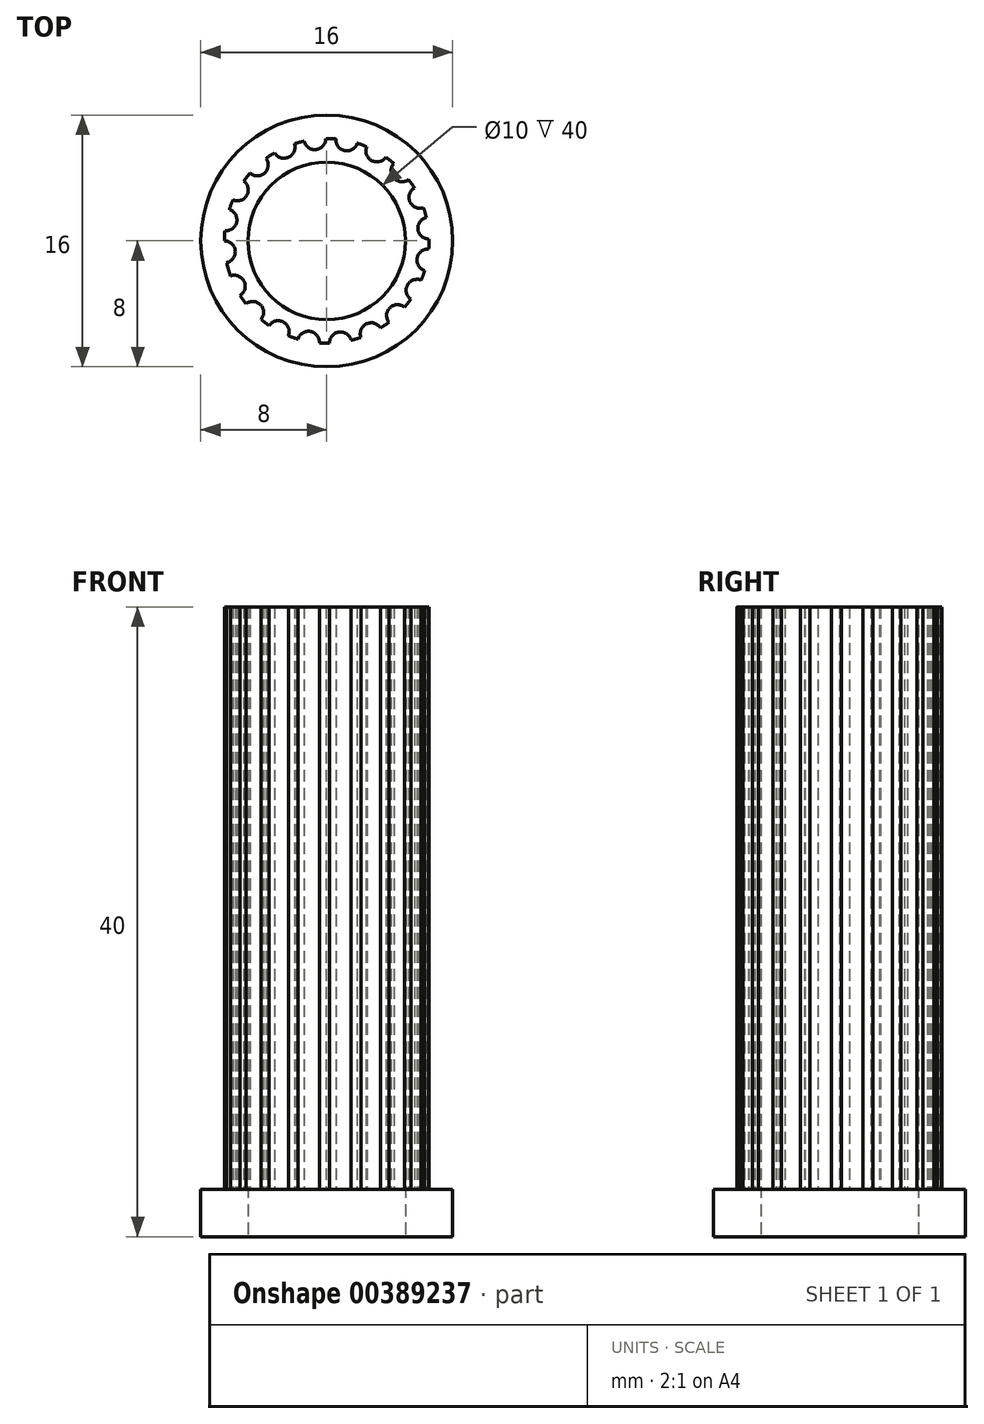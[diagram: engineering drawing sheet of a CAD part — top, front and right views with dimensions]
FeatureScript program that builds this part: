
annotation { "Feature Type Name" : "Feature", "Feature Type Description" : "" }
export const myFeature = defineFeature(function(context is Context, id is Id, definition is map)
    precondition{}
    {
        {
            var Q0;
            Q0=qCreatedBy(makeId("Top.planeOp"),FACE);
            var sketch = newSketch(context, id + "F0", { "sketchPlane" : qUnion([Q0])});
            skCircle(sketch, "E0", {"center": v(0, 0) * mm, "radius": 8 * mm});
            skArc(sketch, "E1", {"start": v(-4.87, 4.3) * mm, "mid": v(-5.08, 4.06) * mm, "end": v(-5.27, 3.8) * mm});
            skCircle(sketch, "E2", {"center": v(0, 0) * mm, "radius": 5 * mm});
            skArc(sketch, "E3", {"start": v(-6.35, -1.38) * mm, "mid": v(-5.8, -0.62) * mm, "end": v(-6.5, 0) * mm});
            skArc(sketch, "E4.1.0", {"start": v(-6.47, 0.64) * mm, "mid": v(-5.72, 1.2) * mm, "end": v(-6.19, 2) * mm});
            skArc(sketch, "E4.2.0", {"start": v(-5.96, 2.6) * mm, "mid": v(-5.08, 2.9) * mm, "end": v(-5.27, 3.8) * mm});
            skArc(sketch, "E4.3.0", {"start": v(-4.87, 4.3) * mm, "mid": v(-3.94, 4.31) * mm, "end": v(-3.85, 5.24) * mm});
            skArc(sketch, "E4.4.0", {"start": v(-3.31, 5.6) * mm, "mid": v(-2.43, 5.32) * mm, "end": v(-2.05, 6.17) * mm});
            skArc(sketch, "E4.5.0", {"start": v(-1.43, 6.34) * mm, "mid": v(-0.67, 5.8) * mm, "end": v(-0.06, 6.5) * mm});
            skArc(sketch, "E4.6.0", {"start": v(0.58, 6.47) * mm, "mid": v(1.14, 5.73) * mm, "end": v(1.94, 6.2) * mm});
            skArc(sketch, "E4.7.0", {"start": v(2.55, 5.98) * mm, "mid": v(2.85, 5.1) * mm, "end": v(3.75, 5.3) * mm});
            skArc(sketch, "E4.8.0", {"start": v(4.26, 4.9) * mm, "mid": v(4.28, 3.98) * mm, "end": v(5.2, 3.9) * mm});
            skArc(sketch, "E4.9.0", {"start": v(5.56, 3.36) * mm, "mid": v(5.3, 2.47) * mm, "end": v(6.15, 2.11) * mm});
            skArc(sketch, "E4.10.0", {"start": v(6.33, 1.5) * mm, "mid": v(5.8, 0.73) * mm, "end": v(6.5, 0.12) * mm});
            skArc(sketch, "E4.11.0", {"start": v(6.48, -0.52) * mm, "mid": v(5.74, -1.09) * mm, "end": v(6.22, -1.88) * mm});
            skArc(sketch, "E4.12.0", {"start": v(6, -2.49) * mm, "mid": v(5.13, -2.8) * mm, "end": v(5.34, -3.7) * mm});
            skArc(sketch, "E4.13.0", {"start": v(4.95, -4.21) * mm, "mid": v(4.02, -4.24) * mm, "end": v(3.95, -5.17) * mm});
            skArc(sketch, "E4.14.0", {"start": v(3.41, -5.53) * mm, "mid": v(2.52, -5.27) * mm, "end": v(2.17, -6.13) * mm});
            skArc(sketch, "E4.15.0", {"start": v(1.55, -6.31) * mm, "mid": v(0.78, -5.8) * mm, "end": v(0.18, -6.5) * mm});
            skArc(sketch, "E4.16.0", {"start": v(-0.47, -6.48) * mm, "mid": v(-1.04, -5.75) * mm, "end": v(-1.83, -6.24) * mm});
            skArc(sketch, "E4.17.0", {"start": v(-2.43, -6.03) * mm, "mid": v(-2.75, -5.15) * mm, "end": v(-3.65, -5.38) * mm});
            skArc(sketch, "E4.18.0", {"start": v(-4.17, -4.99) * mm, "mid": v(-4.2, -4.06) * mm, "end": v(-5.13, -4) * mm});
            skArc(sketch, "E4.19.0", {"start": v(-5.5, -3.46) * mm, "mid": v(-5.25, -2.57) * mm, "end": v(-6.1, -2.22) * mm});
            skLineSegment(sketch, "E4.anchor1", {"start": v(0, 0) * mm, "end": v(-6.35, -1.38) * mm, "construction": true});
            skLineSegment(sketch, "E4.anchor2", {"start": v(0, 0) * mm, "end": v(-5.5, -3.46) * mm, "construction": true});
            skArc(sketch, "E5.trimOffspring", {"start": v(-3.31, 5.6) * mm, "mid": v(-3.59, 5.42) * mm, "end": v(-3.85, 5.24) * mm});
            skArc(sketch, "E6.trimOffspring", {"start": v(-1.43, 6.34) * mm, "mid": v(-1.75, 6.26) * mm, "end": v(-2.05, 6.17) * mm});
            skArc(sketch, "E7.trimOffspring", {"start": v(0.58, 6.47) * mm, "mid": v(0.26, 6.5) * mm, "end": v(-0.06, 6.5) * mm});
            skArc(sketch, "E8.trimOffspring", {"start": v(2.55, 5.98) * mm, "mid": v(2.25, 6.1) * mm, "end": v(1.94, 6.2) * mm});
            skArc(sketch, "E9.trimOffspring", {"start": v(4.26, 4.9) * mm, "mid": v(4.01, 5.11) * mm, "end": v(3.75, 5.3) * mm});
            skArc(sketch, "E10.trimOffspring", {"start": v(5.56, 3.36) * mm, "mid": v(5.39, 3.63) * mm, "end": v(5.2, 3.9) * mm});
            skArc(sketch, "E11.trimOffspring", {"start": v(6.33, 1.5) * mm, "mid": v(6.24, 1.8) * mm, "end": v(6.15, 2.11) * mm});
            skArc(sketch, "E12.trimOffspring", {"start": v(6.48, -0.52) * mm, "mid": v(6.5, -0.2) * mm, "end": v(6.5, 0.12) * mm});
            skArc(sketch, "E13.trimOffspring", {"start": v(6, -2.49) * mm, "mid": v(6.12, -2.19) * mm, "end": v(6.22, -1.88) * mm});
            skArc(sketch, "E14.trimOffspring", {"start": v(4.95, -4.21) * mm, "mid": v(5.15, -3.96) * mm, "end": v(5.34, -3.7) * mm});
            skArc(sketch, "E15.trimOffspring", {"start": v(3.41, -5.53) * mm, "mid": v(3.68, -5.36) * mm, "end": v(3.95, -5.17) * mm});
            skArc(sketch, "E16.trimOffspring", {"start": v(1.55, -6.31) * mm, "mid": v(1.86, -6.23) * mm, "end": v(2.17, -6.13) * mm});
            skArc(sketch, "E17.trimOffspring", {"start": v(-0.47, -6.48) * mm, "mid": v(-0.14, -6.5) * mm, "end": v(0.18, -6.5) * mm});
            skArc(sketch, "E18.trimOffspring", {"start": v(-2.43, -6.03) * mm, "mid": v(-2.13, -6.14) * mm, "end": v(-1.83, -6.24) * mm});
            skArc(sketch, "E19.trimOffspring", {"start": v(-5.96, 2.6) * mm, "mid": v(-6.08, 2.3) * mm, "end": v(-6.19, 2) * mm});
            skArc(sketch, "E20.trimOffspring", {"start": v(-6.47, 0.64) * mm, "mid": v(-6.5, 0.32) * mm, "end": v(-6.5, 0) * mm});
            skArc(sketch, "E21.trimOffspring", {"start": v(-4.17, -4.99) * mm, "mid": v(-3.92, -5.19) * mm, "end": v(-3.65, -5.38) * mm});
            skArc(sketch, "E22.trimOffspring", {"start": v(-5.5, -3.46) * mm, "mid": v(-5.32, -3.73) * mm, "end": v(-5.13, -4) * mm});
            skArc(sketch, "E23.trimOffspring", {"start": v(-6.35, -1.38) * mm, "mid": v(-6.24, -1.8) * mm, "end": v(-6.1, -2.22) * mm});
            skSolve(sketch);
        }
        {
            var Q0;
            Q0=makeQuery(id+"F0.imprint","IMPRINT",FACE,{"disambiguationData":[TD([[makeQuery(id+"F0.imprint","IMPRINT",EDGE,{"derivedFrom":sQuery(id+"F0.wireOp",EDGE,"E1")}),1.0]])]});
            extrude(context, id + "F1", {"entities" : qUnion([Q0]), "depth" : 40 * mm, "offsetDistance" : 25 * mm});
        }
        {
            var Q0;
            Q0=makeQuery(id+"F0.imprint","IMPRINT",FACE,{"disambiguationData":[TD([[makeQuery(id+"F0.imprint","IMPRINT",EDGE,{"derivedFrom":sQuery(id+"F0.wireOp",EDGE,"E0")}),1.0]])]});
            extrude(context, id + "F2", {"entities" : qUnion([Q0]), "operationType" : NewBodyOperationType.ADD, "depth" : 3 * mm, "offsetDistance" : 25 * mm});
        }
    });
